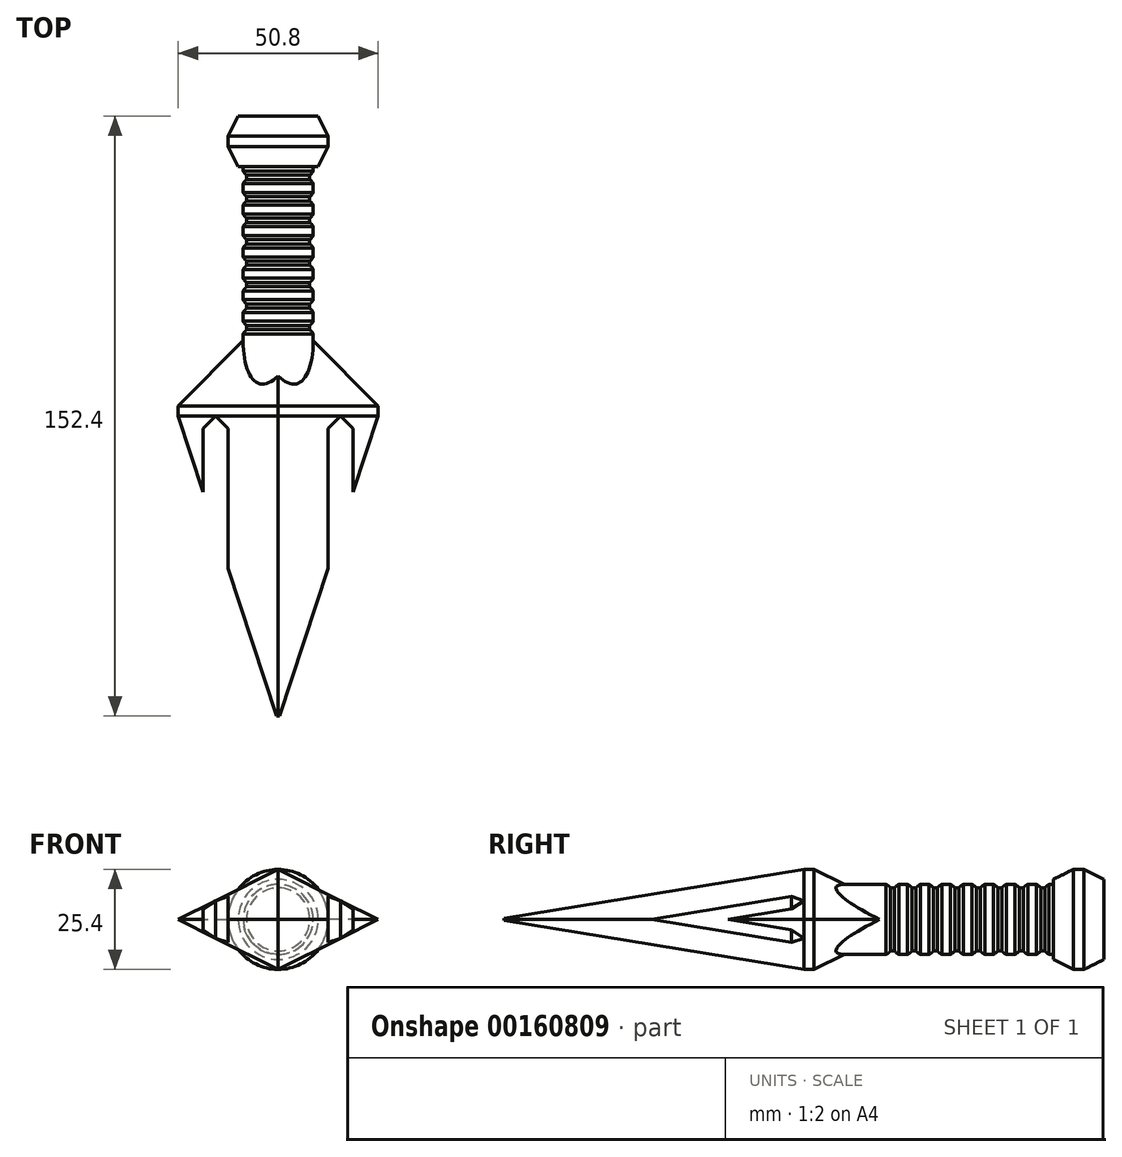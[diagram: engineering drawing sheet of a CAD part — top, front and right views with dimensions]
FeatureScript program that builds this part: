
annotation { "Feature Type Name" : "Feature", "Feature Type Description" : "" }
export const myFeature = defineFeature(function(context is Context, id is Id, definition is map)
    precondition{}
    {
        {
            var Q0;
            Q0=qCreatedBy(makeId("Front.planeOp"),FACE);
            var sketch = newSketch(context, id + "F10", { "sketchPlane" : qUnion([Q0])});
            skLineSegment(sketch, "E0.bottom", {"start": v(25.4, 12.7) * mm, "end": v(-25.4, 12.7) * mm});
            skLineSegment(sketch, "E0.top", {"start": v(25.4, -12.7) * mm, "end": v(-25.4, -12.7) * mm});
            skLineSegment(sketch, "E0.left", {"start": v(25.4, 12.7) * mm, "end": v(25.4, -12.7) * mm});
            skLineSegment(sketch, "E0.right", {"start": v(-25.4, 12.7) * mm, "end": v(-25.4, -12.7) * mm});
            skPoint(sketch, "E0.middle", {"position": v(0, 0) * mm});
            skLineSegment(sketch, "E1", {"start": v(0, 12.7) * mm, "end": v(25.4, 0) * mm});
            skLineSegment(sketch, "E2", {"start": v(25.4, 0) * mm, "end": v(0, -12.7) * mm});
            skLineSegment(sketch, "E3", {"start": v(0, -12.7) * mm, "end": v(0, -12.7) * mm});
            skLineSegment(sketch, "E4", {"start": v(-25.4, 0) * mm, "end": v(0, 12.7) * mm});
            skLineSegment(sketch, "E5", {"start": v(-25.4, 0) * mm, "end": v(0, -12.7) * mm});
            skSolve(sketch);
        }
        {
            var Q0;
            Q0=makeQuery(id+"F10.imprint","IMPRINT",FACE,{"disambiguationData":[TD([[makeQuery(id+"F10.imprint","IMPRINT",EDGE,{"derivedFrom":sQuery(id+"F10.wireOp",EDGE,"E1")}),-1.0]])]});
            extrude(context, id + "F11", {"entities" : qUnion([Q0]), "depth" : 76.2 * mm});
        }
        {
            var Q0;
            Q0=makeQuery(id+"F11.opExtrude","CAP_FACE",FACE,{"disambiguationData":[OSD([sQuery(id+"F10.wireOp",EDGE,"E1"),sQuery(id+"F10.wireOp",EDGE,"E2"),sQuery(id+"F10.wireOp",EDGE,"E4"),sQuery(id+"F10.wireOp",EDGE,"E5")])],"isStart":false});
            chamfer(context, id + "F0", {"entities" : qUnion([Q0]), "chamferType" : ChamferType.TWO_OFFSETS, "width1" : 76.2 * mm, "oppositeDirection" : false, "width2" : 11.18 * mm, "tangentPropagation" : true});
        }
        {
            var Q0;
            Q0=makeQuery(id+"F11.opExtrude","CAP_FACE",FACE,{"disambiguationData":[OSD([sQuery(id+"F10.wireOp",EDGE,"E1"),sQuery(id+"F10.wireOp",EDGE,"E2"),sQuery(id+"F10.wireOp",EDGE,"E4"),sQuery(id+"F10.wireOp",EDGE,"E5")])],"isStart":true});
            extrude(context, id + "F1", {"entities" : qUnion([Q0]), "operationType" : NewBodyOperationType.ADD, "depth" : 25.4 * mm});
        }
        {
            var Q0;
            Q0=makeQuery(id+"F1.opExtrude","CAP_FACE",FACE,{"disambiguationData":[OSD([sQuery(id+"F10.wireOp",EDGE,"E1"),sQuery(id+"F10.wireOp",EDGE,"E2"),sQuery(id+"F10.wireOp",EDGE,"E4"),sQuery(id+"F10.wireOp",EDGE,"E5")])],"isStart":false});
            chamfer(context, id + "F2", {"entities" : qUnion([Q0]), "chamferType" : ChamferType.TWO_OFFSETS, "width1" : 10.16 * mm, "oppositeDirection" : false, "width2" : 22.86 * mm, "tangentPropagation" : true});
        }
        {
            var Q0;
            Q0=qCreatedBy(makeId("Front.planeOp"),FACE);
            var sketch = newSketch(context, id + "F12", { "sketchPlane" : qUnion([Q0])});
            skEllipse(sketch, "E6", {"center": v(0, 0) * mm, "majorRadius": 8.9 * mm, "minorRadius": 8.9 * mm, "majorAxis": v(-1, 0)});
            skSolve(sketch);
        }
        {
            var Q0;
            Q0 = qSketchRegion(id + "F12", true);
            extrude(context, id + "F3", {"entities" : qUnion([Q0]), "operationType" : NewBodyOperationType.ADD, "oppositeDirection" : true, "depth" : 76.2 * mm});
        }
        {
            var Q0;
            Q0=makeQuery(id+"F3.opExtrude","CAP_FACE",FACE,{"disambiguationData":[OSD([sQuery(id+"F12.wireOp",EDGE,"E6")])],"isStart":false});
            chamfer(context, id + "F4", {"entities" : qUnion([Q0]), "width" : 2.54 * mm, "tangentPropagation" : true});
        }
        {
            var Q0;
            Q0=qCreatedBy(makeId("Top.planeOp"),FACE);
            var sketch = newSketch(context, id + "F5", { "sketchPlane" : qUnion([Q0])});
            skLineSegment(sketch, "E7.bottom", {"start": v(19.05, 0) * mm, "end": v(12.7, 0) * mm});
            skLineSegment(sketch, "E7.top", {"start": v(19.05, -61.69) * mm, "end": v(12.7, -61.69) * mm});
            skLineSegment(sketch, "E7.left", {"start": v(19.05, 0) * mm, "end": v(19.05, -61.69) * mm});
            skLineSegment(sketch, "E7.right", {"start": v(12.7, 0) * mm, "end": v(12.7, -61.69) * mm});
            skLineSegment(sketch, "E8.bottom", {"start": v(-12.7, 0) * mm, "end": v(-19.05, 0) * mm});
            skLineSegment(sketch, "E8.top", {"start": v(-12.7, -61.69) * mm, "end": v(-19.05, -61.69) * mm});
            skLineSegment(sketch, "E8.left", {"start": v(-12.7, 0) * mm, "end": v(-12.7, -61.69) * mm});
            skLineSegment(sketch, "E8.right", {"start": v(-19.05, 0) * mm, "end": v(-19.05, -61.69) * mm});
            skSolve(sketch);
        }
        {
            var Q0;
            Q0=makeQuery(id+"F5.imprint","IMPRINT",FACE,{"disambiguationData":[TD([[makeQuery(id+"F5.imprint","IMPRINT",EDGE,{"derivedFrom":sQuery(id+"F5.wireOp",EDGE,"E8.bottom")}),1.0]])]});
            var Q1;
            Q1=makeQuery(id+"F5.imprint","IMPRINT",FACE,{"disambiguationData":[TD([[makeQuery(id+"F5.imprint","IMPRINT",EDGE,{"derivedFrom":sQuery(id+"F5.wireOp",EDGE,"E7.bottom")}),1.0]])]});
            extrude(context, id + "F13", {"entities" : qUnion([Q0, Q1]), "operationType" : NewBodyOperationType.REMOVE, "oppositeDirection" : true, "depth" : 25.4 * mm, "hasSecondDirection" : true, "secondDirectionOppositeDirection" : false, "secondDirectionDepth" : 25.4 * mm});
        }
        {
            var Q0;
            Q0=makeQuery(id+"F13.boolean.opBoolean","COPY",EDGE,{"derivedFrom":makeQuery(id+"F13.opExtrude","SWEPT_EDGE",EDGE,{"disambiguationData":[OSD([sQuery(id+"F5.wireOp",EDGE,"E7.bottom"),sQuery(id+"F5.wireOp",EDGE,"E7.right")])]})});
            var Q1;
            Q1=makeQuery(id+"F13.boolean.opBoolean","COPY",EDGE,{"derivedFrom":makeQuery(id+"F13.opExtrude","SWEPT_EDGE",EDGE,{"disambiguationData":[OSD([sQuery(id+"F5.wireOp",EDGE,"E7.bottom"),sQuery(id+"F5.wireOp",EDGE,"E7.left")])]})});
            var Q2;
            Q2=makeQuery(id+"F13.boolean.opBoolean","COPY",EDGE,{"derivedFrom":makeQuery(id+"F13.opExtrude","SWEPT_EDGE",EDGE,{"disambiguationData":[OSD([sQuery(id+"F5.wireOp",EDGE,"E8.bottom"),sQuery(id+"F5.wireOp",EDGE,"E8.left")])]})});
            var Q3;
            Q3=makeQuery(id+"F13.boolean.opBoolean","COPY",EDGE,{"derivedFrom":makeQuery(id+"F13.opExtrude","SWEPT_EDGE",EDGE,{"disambiguationData":[OSD([sQuery(id+"F5.wireOp",EDGE,"E8.bottom"),sQuery(id+"F5.wireOp",EDGE,"E8.right")])]})});
            chamfer(context, id + "F14", {"entities" : qUnion([Q0, Q1, Q2, Q3]), "width" : 3.17 * mm, "tangentPropagation" : true});
        }
        {
            var Q0;
            Q0=qCreatedBy(makeId("Top.planeOp"),FACE);
            var sketch = newSketch(context, id + "F15", { "sketchPlane" : qUnion([Q0])});
            skLineSegment(sketch, "E9", {"start": v(0, -77.5) * mm, "end": v(0, 78.1) * mm});
            skSolve(sketch);
        }
        {
            var Q0;
            Q0=qCreatedBy(makeId("Top.planeOp"),FACE);
            var sketch = newSketch(context, id + "F16", { "sketchPlane" : qUnion([Q0])});
            skLineSegment(sketch, "E10", {"start": v(-9.13, 19.74) * mm, "end": v(-9.13, 62.22) * mm});
            skArc(sketch, "E11", {"start": v(-8.02, 21.93) * mm, "mid": v(-8.83, 20.96) * mm, "end": v(-9.13, 19.74) * mm});
            skArc(sketch, "E12", {"start": v(-8.02, 27.38) * mm, "mid": v(-9.13, 25.2) * mm, "end": v(-8.02, 23) * mm});
            skArc(sketch, "E13", {"start": v(-8.02, 32.84) * mm, "mid": v(-9.13, 30.64) * mm, "end": v(-8.02, 28.45) * mm});
            skArc(sketch, "E14", {"start": v(-8.02, 38.3) * mm, "mid": v(-9.13, 36.1) * mm, "end": v(-8.02, 33.9) * mm});
            skArc(sketch, "E15", {"start": v(-8.02, 43.75) * mm, "mid": v(-9.13, 41.55) * mm, "end": v(-8.02, 39.36) * mm});
            skArc(sketch, "E16", {"start": v(-8.02, 49.2) * mm, "mid": v(-9.13, 47) * mm, "end": v(-8.02, 44.82) * mm});
            skArc(sketch, "E17", {"start": v(-8.02, 54.66) * mm, "mid": v(-9.13, 52.46) * mm, "end": v(-8.02, 50.27) * mm});
            skLineSegment(sketch, "E18", {"start": v(-6.4, 60.65) * mm, "end": v(-6.4, 60.65) * mm});
            skLineSegment(sketch, "E19", {"start": v(-9.13, 62.22) * mm, "end": v(-9.13, 63.37) * mm});
            skArc(sketch, "E20", {"start": v(-9.13, 63.37) * mm, "mid": v(-8.83, 62.14) * mm, "end": v(-8.02, 61.18) * mm});
            skLineSegment(sketch, "E21", {"start": v(-8.02, 21.93) * mm, "end": v(-8.02, 23) * mm});
            skArc(sketch, "E22.trimOffspring", {"start": v(-8.02, 60.11) * mm, "mid": v(-9.13, 57.92) * mm, "end": v(-8.02, 55.72) * mm});
            skLineSegment(sketch, "E23.trimOffspring", {"start": v(-8.02, 60.11) * mm, "end": v(-8.02, 61.18) * mm});
            skLineSegment(sketch, "E24.trimOffspring", {"start": v(-8.02, 54.66) * mm, "end": v(-8.02, 55.72) * mm});
            skLineSegment(sketch, "E25.trimOffspring", {"start": v(-8.02, 49.2) * mm, "end": v(-8.02, 50.27) * mm});
            skLineSegment(sketch, "E26.trimOffspring", {"start": v(-8.02, 43.75) * mm, "end": v(-8.02, 44.82) * mm});
            skLineSegment(sketch, "E27.trimOffspring", {"start": v(-8.02, 38.3) * mm, "end": v(-8.02, 39.36) * mm});
            skLineSegment(sketch, "E28.trimOffspring", {"start": v(-8.02, 32.84) * mm, "end": v(-8.02, 33.9) * mm});
            skLineSegment(sketch, "E29.trimOffspring", {"start": v(-8.02, 27.38) * mm, "end": v(-8.02, 28.45) * mm});
            skSolve(sketch);
        }
        {
            var Q0;
            {var subQ4=sQuery(id+"F16.wireOp",EDGE,"E19");Q0=makeQuery(id+"F16.imprint","IMPRINT",FACE,{"disambiguationData":[TD([[makeQuery(id+"F16.imprint","IMPRINT",EDGE,{"derivedFrom":subQ4}),-1.0]])]});}
            var Q1;
            {var subQ5=sQuery(id+"F16.wireOp",EDGE,"E24.trimOffspring");Q1=makeQuery(id+"F16.imprint","IMPRINT",FACE,{"disambiguationData":[TD([[makeQuery(id+"F16.imprint","IMPRINT",EDGE,{"derivedFrom":subQ5}),1.0]])]});}
            var Q2;
            {var subQ5=sQuery(id+"F16.wireOp",EDGE,"E25.trimOffspring");Q2=makeQuery(id+"F16.imprint","IMPRINT",FACE,{"disambiguationData":[TD([[makeQuery(id+"F16.imprint","IMPRINT",EDGE,{"derivedFrom":subQ5}),1.0]])]});}
            var Q3;
            {var subQ5=sQuery(id+"F16.wireOp",EDGE,"E26.trimOffspring");Q3=makeQuery(id+"F16.imprint","IMPRINT",FACE,{"disambiguationData":[TD([[makeQuery(id+"F16.imprint","IMPRINT",EDGE,{"derivedFrom":subQ5}),1.0]])]});}
            var Q4;
            {var subQ5=sQuery(id+"F16.wireOp",EDGE,"E27.trimOffspring");Q4=makeQuery(id+"F16.imprint","IMPRINT",FACE,{"disambiguationData":[TD([[makeQuery(id+"F16.imprint","IMPRINT",EDGE,{"derivedFrom":subQ5}),1.0]])]});}
            var Q5;
            {var subQ5=sQuery(id+"F16.wireOp",EDGE,"E28.trimOffspring");Q5=makeQuery(id+"F16.imprint","IMPRINT",FACE,{"disambiguationData":[TD([[makeQuery(id+"F16.imprint","IMPRINT",EDGE,{"derivedFrom":subQ5}),1.0]])]});}
            var Q6;
            {var subQ5=sQuery(id+"F16.wireOp",EDGE,"E29.trimOffspring");Q6=makeQuery(id+"F16.imprint","IMPRINT",FACE,{"disambiguationData":[TD([[makeQuery(id+"F16.imprint","IMPRINT",EDGE,{"derivedFrom":subQ5}),1.0]])]});}
            var Q7;
            {var subQ0=sQuery(id+"F16.wireOp",EDGE,"E11");Q7=makeQuery(id+"F16.imprint","IMPRINT",FACE,{"disambiguationData":[TD([[makeQuery(id+"F16.imprint","IMPRINT",EDGE,{"derivedFrom":subQ0}),-1.0]])]});}
            var Q8;
            Q8=sQuery(id+"F15.wireOp",EDGE,"E9");
            revolve(context, id + "F6", {"operationType" : NewBodyOperationType.REMOVE, "entities" : qUnion([Q0, Q1, Q2, Q3, Q4, Q5, Q6, Q7]), "axis" : qUnion([Q8]), "revolveType" : RevolveType.FULL, "oppositeDirection" : true});
        }
        {
            var Q0;
            Q0=makeQuery(id+"F3.opExtrude","CAP_FACE",FACE,{"disambiguationData":[OSD([sQuery(id+"F12.wireOp",EDGE,"E6")])],"isStart":false});
            var sketch = newSketch(context, id + "F7", { "sketchPlane" : qUnion([Q0])});
            skCircle(sketch, "E30", {"center": v(0, 0) * mm, "radius": 12.7 * mm});
            skSolve(sketch);
        }
        {
            var Q0;
            Q0=makeQuery(id+"F7.imprint","IMPRINT",FACE,{"disambiguationData":[TD([[makeQuery(id+"F7.imprint","IMPRINT",EDGE,{"derivedFrom":sQuery(id+"F7.wireOp",EDGE,"E30")}),1.0]])]});
            var Q1;
            {var subQ0=sQuery(id+"F12.wireOp",EDGE,"E6");Q1=makeQuery(id+"F7.imprint","IMPRINT",FACE,{"disambiguationData":[TD([[makeQuery(id+"F7.imprint","IMPRINT",EDGE,{"derivedFrom":makeQuery(id+"F4.opChamfer","BLEND_EDGE",EDGE,{"blendedFrom":[makeQuery(id+"F3.opExtrude","CAP_EDGE",EDGE,{"disambiguationData":[OSD([subQ0])],"isStart":false}),makeQuery(id+"F3.opExtrude","CAP_FACE",FACE,{"disambiguationData":[OSD([subQ0])],"isStart":false})],"blendedInto":[makeQuery(id+"F3.opExtrude","CAP_FACE",FACE,{"disambiguationData":[OSD([subQ0])],"isStart":false})]})}),1.0]])]});}
            extrude(context, id + "F8", {"entities" : qUnion([Q0, Q1]), "operationType" : NewBodyOperationType.ADD, "oppositeDirection" : true, "depth" : 12.9 * mm});
        }
        {
            var Q0;
            Q0=makeQuery(id+"F8.opExtrude","CAP_EDGE",EDGE,{"disambiguationData":[OSD([sQuery(id+"F7.wireOp",EDGE,"E30")])],"isStart":false});
            var Q1;
            Q1=makeQuery(id+"F8.opExtrude","CAP_EDGE",EDGE,{"disambiguationData":[OSD([sQuery(id+"F7.wireOp",EDGE,"E30")])],"isStart":true});
            chamfer(context, id + "F9", {"entities" : qUnion([Q0, Q1]), "chamferType" : ChamferType.TWO_OFFSETS, "width1" : 5.08 * mm, "oppositeDirection" : false, "width2" : 2.54 * mm, "tangentPropagation" : true});
        }
    });
